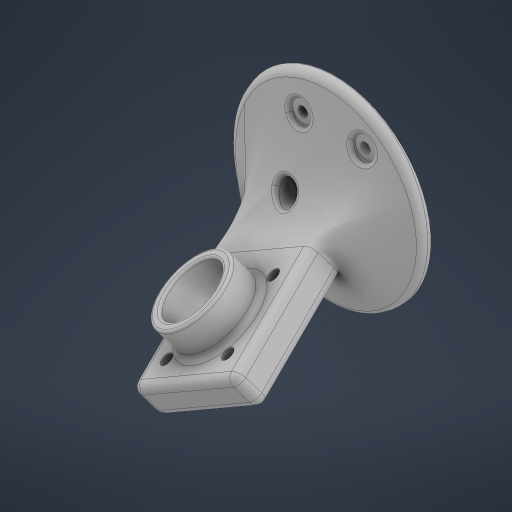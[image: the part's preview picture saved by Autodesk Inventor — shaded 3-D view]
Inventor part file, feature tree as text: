
AUTODESK INVENTOR PART (.ipt)
format: ipt  version: 2023 (Build 270158000, 158)  size: 733,184 bytes
history: native  units: in
note: dims shown in document units (in); Inventor stores cm internally (conversion verified against a paired STEP export)
features: extrude x1, sketch x1, other x1
ambient origin geometry x8: Origin, YZ Plane, XZ Plane, XY Plane, X Axis, Y Axis, Z Axis, Center Point
bodies: Solid1 (feature_tree)
feature tree (3):
  extrude  "Extrusion1"  [1 undecoded]
  sketch  "Sketch1"  dims[d0=0.3937in d1=0.0in]
  other  "6328-24b-1010 Left Wide Angle Camera Mount"
note: 1 required parameter value undecoded (feature->parameter linkage not recoverable at this tier; creation-order binding heuristic only, values carry confidence <= 0.55)
